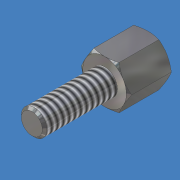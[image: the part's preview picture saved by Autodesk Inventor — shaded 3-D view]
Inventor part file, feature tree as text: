
AUTODESK INVENTOR PART (.ipt)
format: ipt  version: unknown  size: 220,672 bytes
history: native  units: mm (DEFAULTED — no unit token found)
features: sketch x4, extrude x2, chamfer x2, revolve x1, mirror x1, thread x1, hole x1
ambient origin geometry x8: Origin, YZ Plane, XZ Plane, XY Plane, X Axis, Y Axis, Z Axis, Center Point
feature tree (12):
  extrude  "Extrusion1"  Depth=4.7498mm TaperAngle=0.0deg
  revolve  "Revolution1"  [1 undecoded]
  mirror  "Mirror1"
  extrude  "Extrusion2"  Depth=25.4mm TaperAngle=0.0deg
  chamfer  "Chamfer1"  Angle=60.0deg  [1 undecoded]
  thread  "Thread1"  [1 undecoded]
  hole  "Hole1"  [1 undecoded]
  chamfer  "Chamfer2"  [1 undecoded]
  sketch  "Sketch1"  dims[d0=4.7498mm d1=4.7498mm d2=0.0mm]
  sketch  "Sketch2"  dims[d3=2.794mm d4=7.9375mm d5=0.0mm]
  sketch  "Sketch3"  dims[d6=0.254mm d7=3.175mm d8=25.4mm d9=0.0mm]
  sketch  "Sketch4"  dims[d11=90.0deg d12=60.0deg d13=2.159mm d14=5.08mm d15=9.525mm d16=6.35mm d17=14.3117mm d18=6.35mm d19=20.594885mm d20=0.254mm d21=3.175mm d22=45.0deg d23=45.0deg]
note: 5 required parameter values undecoded (feature->parameter linkage not recoverable at this tier; creation-order binding heuristic only, values carry confidence <= 0.55)